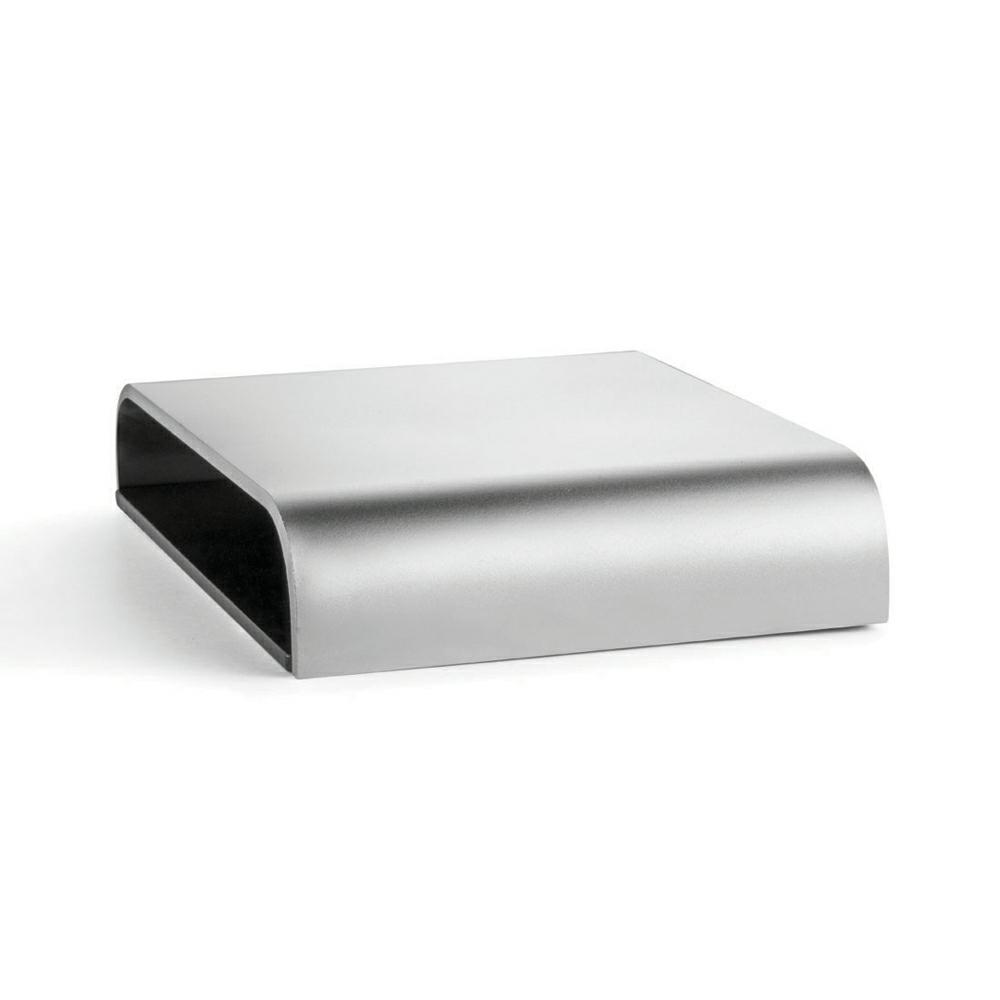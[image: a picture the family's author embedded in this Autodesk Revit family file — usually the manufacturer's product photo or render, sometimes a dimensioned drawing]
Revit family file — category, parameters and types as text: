
# Revit family: Platek_Passo
name_source: partatom
category: Apparecchi per illuminazione
revit_build: Autodesk Revit 2017 (Build: 20160225_1515(x64)
units: mm (PartAtom-declared; Revit-internal decimal feet)

## family parameters
Basato su piano di lavoro = Sì
Condiviso = No
Punto di calcolo locali = No
Quota connettore circolare = Usa diametro
Sempre verticale = No
Sorgente d'illuminazione = Sì
Taglio con vuoti quando caricato = No
Tipo di parte = Normale

## types (2) — shared parameters
Aluminium = PLK_Aluminium
Angolo inclinazione = 90.00°
Beam Angle = 0.00°
Body2 = PLK_Corten Steel
CRI = >80
Carico apparente = 0 VA
Colour Temperature = 3000 K
Commenti sul tipo = Walls, Pedestrian areas, Paths, Roads
Descrizione = Outdoor Lighting, Floor/Ground Illumination
Diffuse Type = Transparent Glass
Dimmable = No
Emetti da larghezza rettangolo = 15 mm  [stored 0.0492126 ft]
Emetti da lunghezza rettangolo = 55 mm  [stored 0.180446 ft]
Energy Efficiency Rating = A/A+/A++
Filtro dei colori = 16777215
IK Rating = IK 10
IP Rating = IP67
Insulation Class = 3
LED Protection = Power supply excluded to be ordered separately
Lampada = LED
Light Source = PLK_Light Source
Luminaire Luminous Flux = 89 lm
Luminaire Luminous Intensity = 124 cd
Luminaire Wattage = 8 W
Manufacturer Comment = 3mm flat tempered extra clear glass
Modello = PASSO
Mounting Type = Ground/Wall
Nota chiave = Other Led colors available on request
PLATEK FInishes = Painted Aluminium Avalaible in Anthracite/Black/White/Corten/Bronze
Power Supply Unit = Excluded
Product Dimension = L110mm x L145mm x H28mm
Product Documentation Link = http://www.platek.eu
Product Page URL = http://www.platek.eu
Produttore = PLATEK SRL
Prospetto di default = 1219.2 mm  [stored 4 ft]
Rendi la forma visibile nel rendering = No
Supply Voltage = 24 V
URL = www.platek.eu
Variazione temperatura colore lampada con luminosità attenuata = <Nessuno>

## per-type parameters (varying)
| type | Body | Codice assieme | File diagramma fotometrico | Immagine tipo | PLATEK Article Code |
| 9404711_7,5W_LED_3000K | PLK_Corten Steel | 9404711 | 9404711.IES | passo_corten.jpg | 9404711 |
| 9404411_7,5W_LED_3000K | PLK_Grey | 9404411 | 9404411.IES | passo_inox.jpg | 9404411 |

note: [stored X ft] marks values corroborated as IEEE doubles in the binary element streams (Revit-internal decimal feet)
